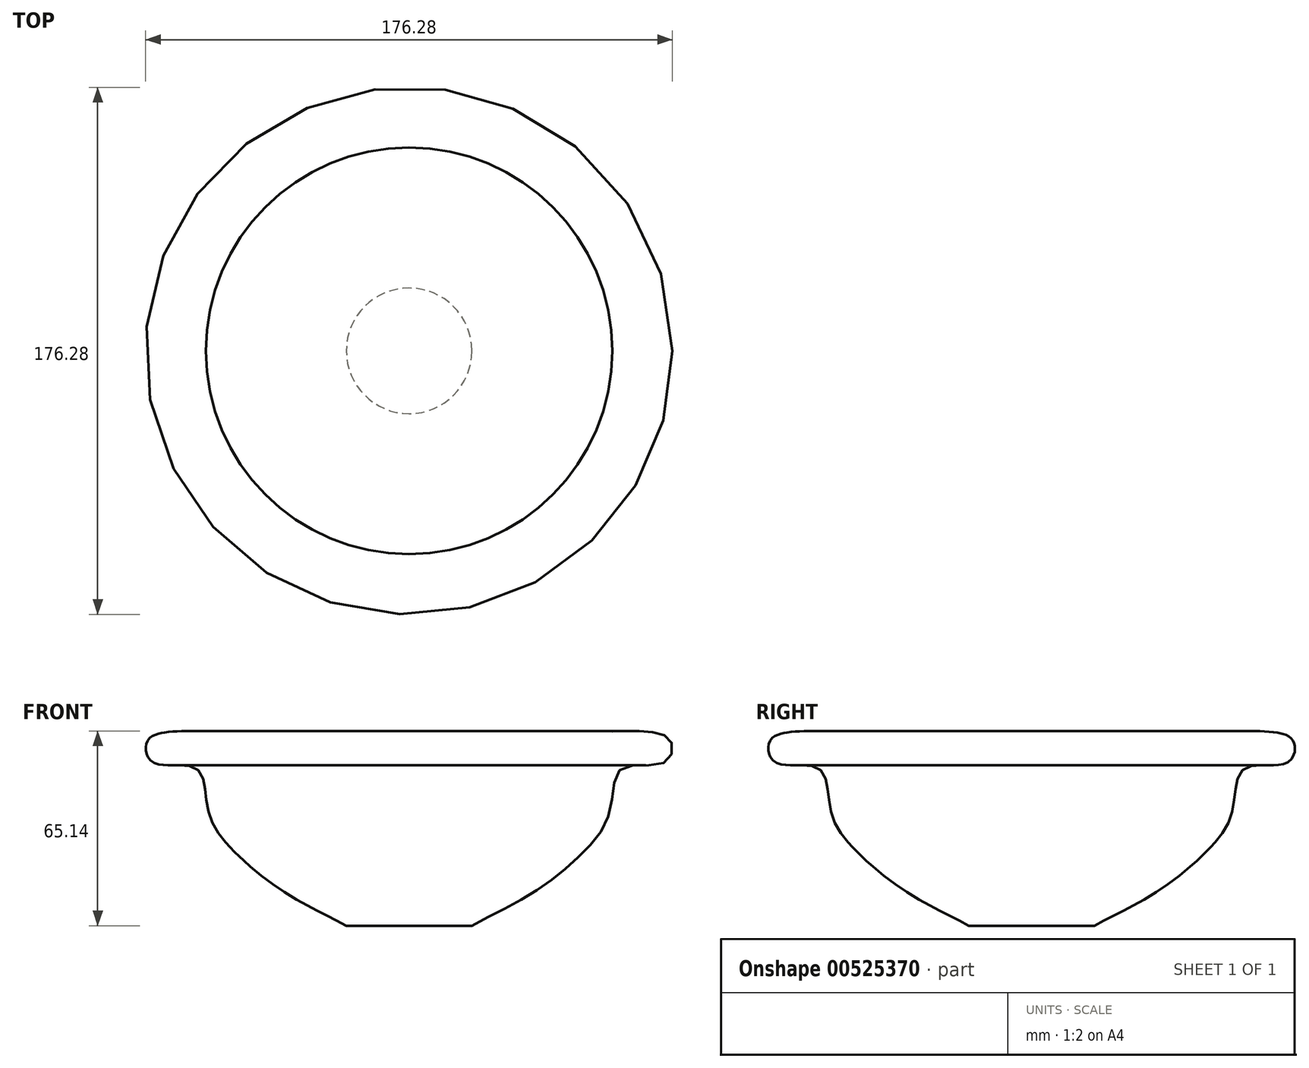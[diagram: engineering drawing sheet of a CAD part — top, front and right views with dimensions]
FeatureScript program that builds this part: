
annotation { "Feature Type Name" : "Feature", "Feature Type Description" : "" }
export const myFeature = defineFeature(function(context is Context, id is Id, definition is map)
    precondition{}
    {
        {
            var Q0;
            Q0=qCreatedBy(makeId("Front.planeOp"),FACE);
            var sketch = newSketch(context, id + "F0", { "sketchPlane" : qUnion([Q0])});
            skLineSegment(sketch, "E0", {"start": v(0, 0) * mm, "end": v(21, 0) * mm});
            skFitSpline(sketch, "E1", {"points": [v(21, 0) * mm, v(40.62, 10.53) * mm, v(56.65, 22.98) * mm, v(67.08, 37.93) * mm, v(71.18, 52.54) * mm, v(85.64, 54.64) * mm, v(87.53, 61.82) * mm, v(79.81, 64.87) * mm, v(68, 65) * mm], "startDerivative": vector(120.05, 64.9) * mm, "endDerivative": vector(-104.01, -4.92) * mm});
            skLineSegment(sketch, "E2", {"start": v(68, 65) * mm, "end": v(0, 65) * mm});
            skLineSegment(sketch, "E3", {"start": v(0, 65) * mm, "end": v(0, 0) * mm});
            skSolve(sketch);
        }
        {
            var Q0;
            Q0=makeQuery(id+"F0.imprint","IMPRINT",FACE,{"disambiguationData":[TD([[makeQuery(id+"F0.imprint","IMPRINT",EDGE,{"derivedFrom":sQuery(id+"F0.wireOp",EDGE,"E0")}),1.0]])]});
            var Q1;
            Q1=sQuery(id+"F0.wireOp",EDGE,"E3");
            revolve(context, id + "F1", {"entities" : qUnion([Q0]), "axis" : qUnion([Q1]), "revolveType" : RevolveType.FULL});
        }
    });
